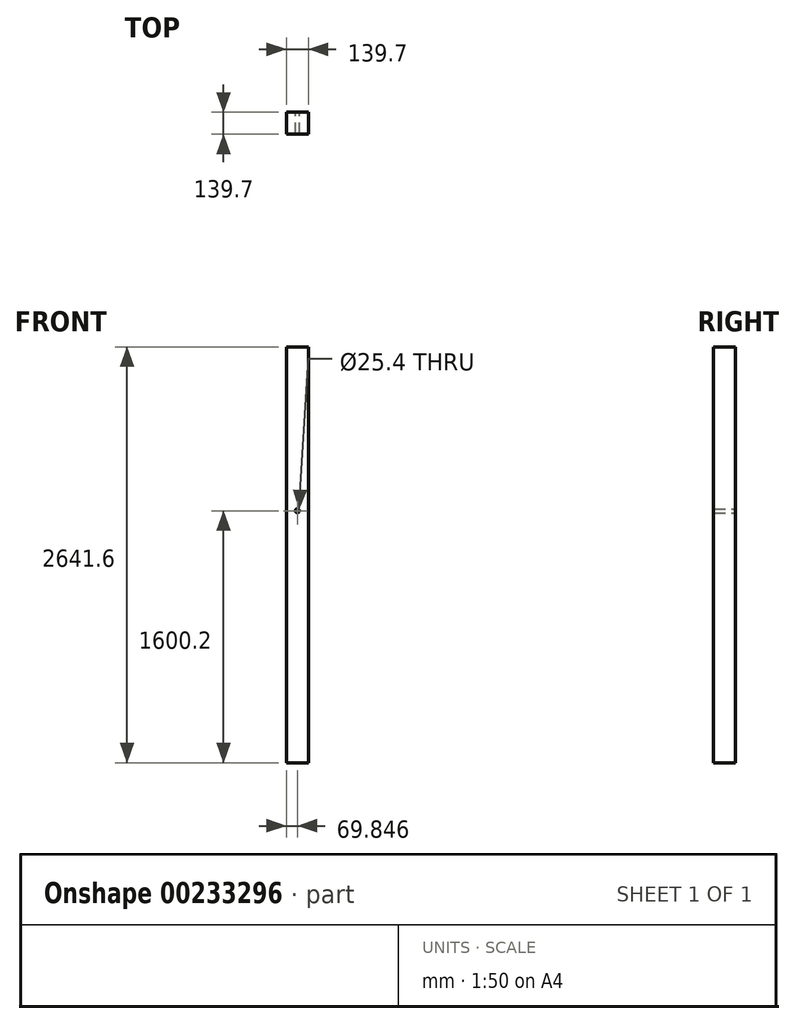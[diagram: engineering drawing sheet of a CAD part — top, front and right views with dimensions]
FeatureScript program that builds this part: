
annotation { "Feature Type Name" : "Feature", "Feature Type Description" : "" }
export const myFeature = defineFeature(function(context is Context, id is Id, definition is map)
    precondition{}
    {
        {
            var Q0;
            Q0=qCreatedBy(makeId("Front.planeOp"),FACE);
            var sketch = newSketch(context, id + "F0", { "sketchPlane" : qUnion([Q0])});
            skLineSegment(sketch, "E0.bottom", {"start": v(-528.34, 2110.87) * mm, "end": v(-388.64, 2110.87) * mm});
            skLineSegment(sketch, "E0.top", {"start": v(-528.34, -530.73) * mm, "end": v(-388.64, -530.73) * mm});
            skLineSegment(sketch, "E0.left", {"start": v(-528.34, 2110.87) * mm, "end": v(-528.34, -530.73) * mm});
            skLineSegment(sketch, "E0.right", {"start": v(-388.64, 2110.87) * mm, "end": v(-388.64, -530.73) * mm});
            skCircle(sketch, "E1", {"center": v(-458.5, 1069.47) * mm, "radius": 12.7 * mm});
            skSolve(sketch);
        }
        {
            var Q0;
            Q0=makeQuery(id+"F0.imprint","IMPRINT",FACE,{"disambiguationData":[TD([[makeQuery(id+"F0.imprint","IMPRINT",EDGE,{"derivedFrom":sQuery(id+"F0.wireOp",EDGE,"E0.bottom")}),-1.0]])]});
            extrude(context, id + "F1", {"entities" : qUnion([Q0]), "depth" : 139.7 * mm});
        }
    });
